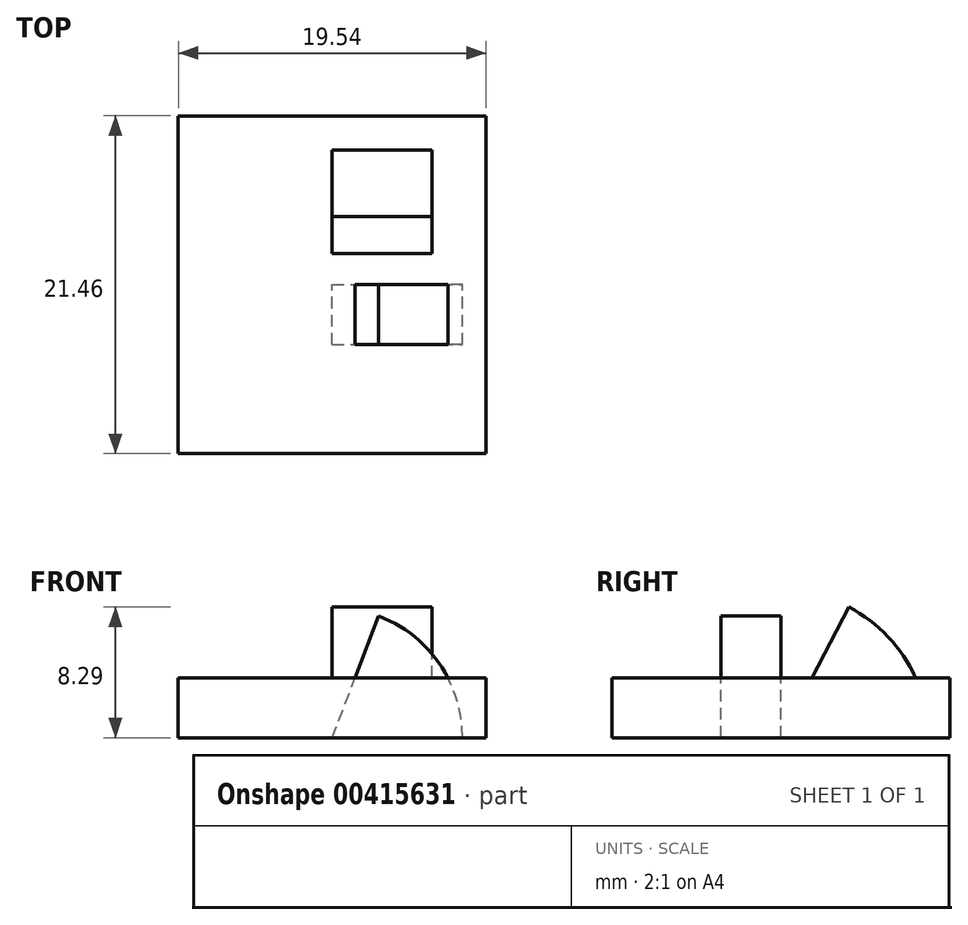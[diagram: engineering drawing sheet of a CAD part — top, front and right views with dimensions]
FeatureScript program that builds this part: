
annotation { "Feature Type Name" : "Feature", "Feature Type Description" : "" }
export const myFeature = defineFeature(function(context is Context, id is Id, definition is map)
    precondition{}
    {
        {
            var Q0;
            Q0=qCreatedBy(makeId("Top.planeOp"),FACE);
            var sketch = newSketch(context, id + "F0", { "sketchPlane" : qUnion([Q0])});
            skLineSegment(sketch, "E0.bottom", {"start": v(9.77, 10.73) * mm, "end": v(-9.77, 10.73) * mm});
            skLineSegment(sketch, "E0.top", {"start": v(9.77, -10.73) * mm, "end": v(-9.77, -10.73) * mm});
            skLineSegment(sketch, "E0.left", {"start": v(9.77, 10.73) * mm, "end": v(9.77, -10.73) * mm});
            skLineSegment(sketch, "E0.right", {"start": v(-9.77, 10.73) * mm, "end": v(-9.77, -10.73) * mm});
            skPoint(sketch, "E0.middle", {"position": v(0, 0) * mm});
            skSolve(sketch);
        }
        {
            var Q0;
            Q0 = qSketchRegion(id + "F0", true);
            extrude(context, id + "F1", {"entities" : qUnion([Q0]), "depth" : 3.8 * mm});
        }
        {
            var Q0;
            Q0=qCreatedBy(makeId("Right.planeOp"),FACE);
            var sketch = newSketch(context, id + "F2", { "sketchPlane" : qUnion([Q0])});
            skArc(sketch, "E1", {"start": v(4.32, 8.3) * mm, "mid": v(8, 4.85) * mm, "end": v(9.35, 0) * mm});
            skLineSegment(sketch, "E2", {"start": v(0, 0) * mm, "end": v(4.32, 8.3) * mm});
            skLineSegment(sketch, "E3", {"start": v(0, 0) * mm, "end": v(9.35, 0) * mm});
            skSolve(sketch);
        }
        {
            var Q0;
            Q0 = qSketchRegion(id + "F2", true);
            extrude(context, id + "F3", {"entities" : qUnion([Q0]), "operationType" : NewBodyOperationType.ADD, "depth" : 6.35 * mm});
        }
        {
            var Q0;
            Q0=qCreatedBy(makeId("Front.planeOp"),FACE);
            var sketch = newSketch(context, id + "F4", { "sketchPlane" : qUnion([Q0])});
            skArc(sketch, "E4", {"start": v(2.95, 7.73) * mm, "mid": v(6.81, 4.7) * mm, "end": v(8.27, 0) * mm});
            skLineSegment(sketch, "E5", {"start": v(0, 0) * mm, "end": v(2.95, 7.73) * mm});
            skLineSegment(sketch, "E6", {"start": v(0, 0) * mm, "end": v(8.27, 0) * mm});
            skSolve(sketch);
        }
        {
            var Q0;
            Q0 = qSketchRegion(id + "F4", true);
            extrude(context, id + "F5", {"entities" : qUnion([Q0]), "depth" : 3.8 * mm});
        }
    });
